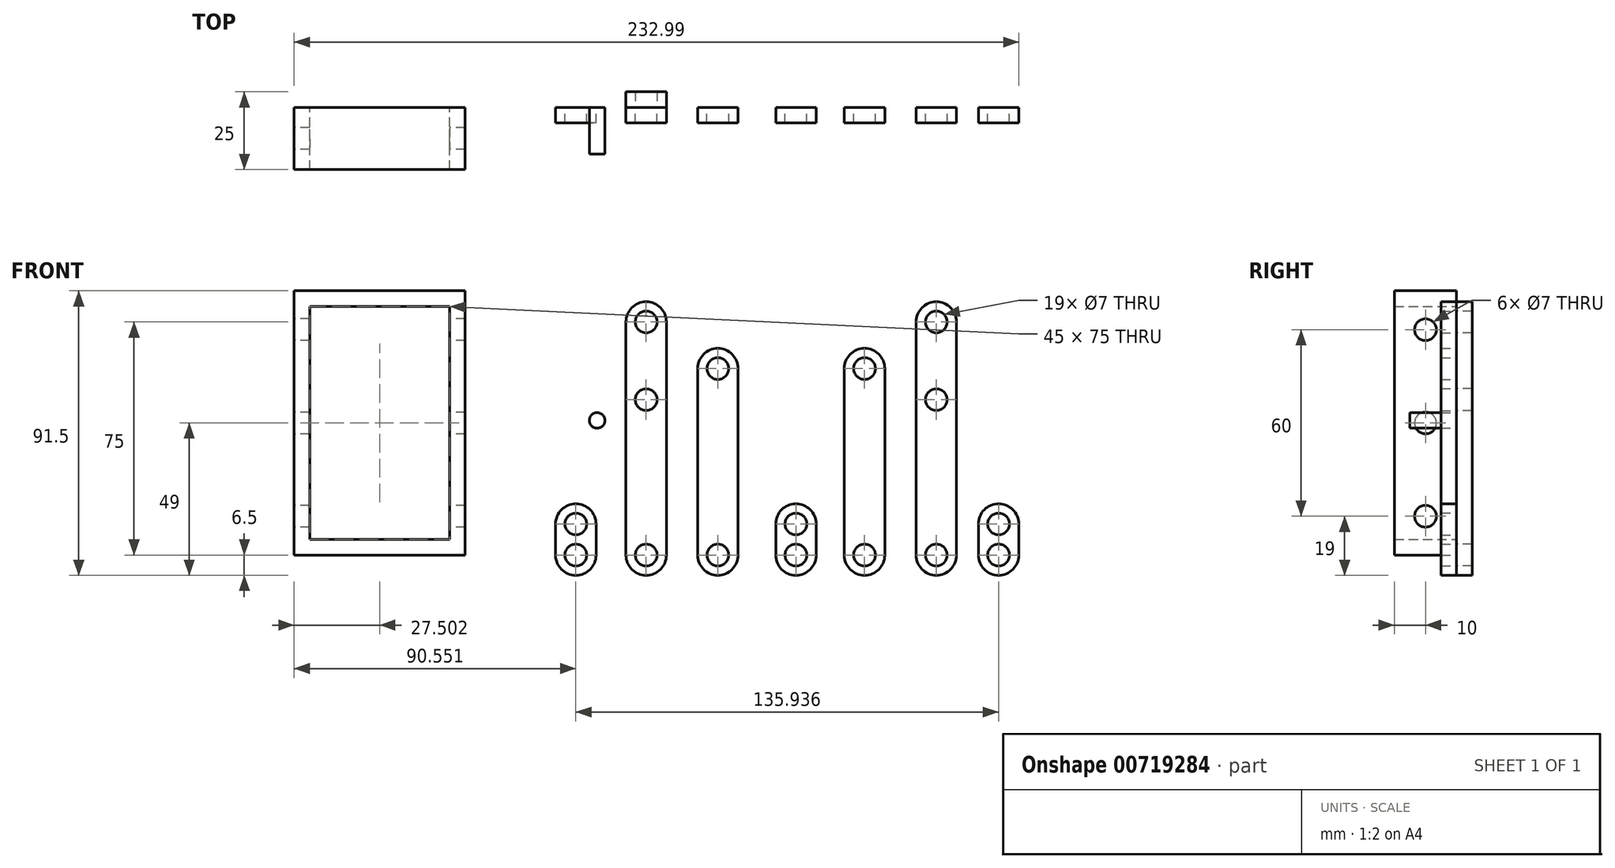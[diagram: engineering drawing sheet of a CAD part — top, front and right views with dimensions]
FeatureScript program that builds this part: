
annotation { "Feature Type Name" : "Feature", "Feature Type Description" : "" }
export const myFeature = defineFeature(function(context is Context, id is Id, definition is map)
    precondition{}
    {
        {
            assignVariable(context, id + "F0", {"name" : "D", "anyValue" : 5});
        }
        {
            var Q0;
            Q0=qCreatedBy(makeId("Front.planeOp"),FACE);
            var sketch = newSketch(context, id + "F1", { "sketchPlane" : qUnion([Q0])});
            skLineSegment(sketch, "E0", {"start": v(3.36, 0) * mm, "end": v(3.36, 10) * mm});
            skLineSegment(sketch, "E1", {"start": v(16.36, 10) * mm, "end": v(16.36, 0) * mm});
            skArc(sketch, "E2", {"start": v(16.36, 10) * mm, "mid": v(9.86, 16.5) * mm, "end": v(3.36, 10) * mm});
            skArc(sketch, "E3", {"start": v(3.36, 0) * mm, "mid": v(9.86, -6.5) * mm, "end": v(16.36, 0) * mm});
            skCircle(sketch, "E4", {"center": v(9.86, 10) * mm, "radius": 3.5 * mm});
            skCircle(sketch, "E5", {"center": v(9.86, 0) * mm, "radius": 3.5 * mm});
            skLineSegment(sketch, "E6", {"start": v(25.98, 0) * mm, "end": v(25.98, 75) * mm});
            skLineSegment(sketch, "E7", {"start": v(38.98, 75) * mm, "end": v(38.98, 0) * mm});
            skArc(sketch, "E8", {"start": v(38.98, 75) * mm, "mid": v(32.48, 81.5) * mm, "end": v(25.98, 75) * mm});
            skArc(sketch, "E9", {"start": v(25.98, 0) * mm, "mid": v(32.48, -6.5) * mm, "end": v(38.98, 0) * mm});
            skCircle(sketch, "E10", {"center": v(32.48, 75) * mm, "radius": 3.5 * mm});
            skCircle(sketch, "E11", {"center": v(32.48, 0) * mm, "radius": 3.5 * mm});
            skCircle(sketch, "E12", {"center": v(32.48, 50) * mm, "radius": 3.5 * mm});
            skLineSegment(sketch, "E13", {"start": v(49.03, 0) * mm, "end": v(49.03, 60) * mm});
            skLineSegment(sketch, "E14", {"start": v(62.03, 60) * mm, "end": v(62.03, 0) * mm});
            skArc(sketch, "E15", {"start": v(62.03, 60) * mm, "mid": v(55.53, 66.5) * mm, "end": v(49.03, 60) * mm});
            skArc(sketch, "E16", {"start": v(49.03, 0) * mm, "mid": v(55.53, -6.5) * mm, "end": v(62.03, 0) * mm});
            skCircle(sketch, "E17", {"center": v(55.53, 60) * mm, "radius": 3.5 * mm});
            skCircle(sketch, "E18", {"center": v(55.53, 0) * mm, "radius": 3.5 * mm});
            skLineSegment(sketch, "E19", {"start": v(74.13, 0) * mm, "end": v(74.13, 10) * mm});
            skLineSegment(sketch, "E20", {"start": v(87.13, 10) * mm, "end": v(87.13, 0) * mm});
            skArc(sketch, "E21", {"start": v(87.13, 10) * mm, "mid": v(80.63, 16.5) * mm, "end": v(74.13, 10) * mm});
            skArc(sketch, "E22", {"start": v(74.13, 0) * mm, "mid": v(80.63, -6.5) * mm, "end": v(87.13, 0) * mm});
            skCircle(sketch, "E23", {"center": v(80.63, 10) * mm, "radius": 3.5 * mm});
            skCircle(sketch, "E24", {"center": v(80.63, 0) * mm, "radius": 3.5 * mm});
            skLineSegment(sketch, "E25", {"start": v(96.2, 0) * mm, "end": v(96.2, 60) * mm});
            skLineSegment(sketch, "E26", {"start": v(109.2, 60) * mm, "end": v(109.2, 0) * mm});
            skArc(sketch, "E27", {"start": v(109.2, 60) * mm, "mid": v(102.7, 66.5) * mm, "end": v(96.2, 60) * mm});
            skArc(sketch, "E28", {"start": v(96.2, 0) * mm, "mid": v(102.7, -6.5) * mm, "end": v(109.2, 0) * mm});
            skCircle(sketch, "E29", {"center": v(102.7, 60) * mm, "radius": 3.5 * mm});
            skCircle(sketch, "E30", {"center": v(102.7, 0) * mm, "radius": 3.5 * mm});
            skLineSegment(sketch, "E31", {"start": v(119.27, 0) * mm, "end": v(119.27, 75) * mm});
            skLineSegment(sketch, "E32", {"start": v(132.27, 75) * mm, "end": v(132.27, 0) * mm});
            skArc(sketch, "E33", {"start": v(132.27, 75) * mm, "mid": v(125.77, 81.5) * mm, "end": v(119.27, 75) * mm});
            skArc(sketch, "E34", {"start": v(119.27, 0) * mm, "mid": v(125.77, -6.5) * mm, "end": v(132.27, 0) * mm});
            skCircle(sketch, "E35", {"center": v(125.77, 75) * mm, "radius": 3.5 * mm});
            skCircle(sketch, "E36", {"center": v(125.77, 0) * mm, "radius": 3.5 * mm});
            skCircle(sketch, "E37", {"center": v(125.77, 50) * mm, "radius": 3.5 * mm});
            skLineSegment(sketch, "E38", {"start": v(139.3, 0) * mm, "end": v(139.3, 10) * mm});
            skLineSegment(sketch, "E39", {"start": v(152.3, 10) * mm, "end": v(152.3, 0) * mm});
            skArc(sketch, "E40", {"start": v(152.3, 10) * mm, "mid": v(145.8, 16.5) * mm, "end": v(139.3, 10) * mm});
            skArc(sketch, "E41", {"start": v(139.3, 0) * mm, "mid": v(145.8, -6.5) * mm, "end": v(152.3, 0) * mm});
            skCircle(sketch, "E42", {"center": v(145.8, 10) * mm, "radius": 3.5 * mm});
            skCircle(sketch, "E43", {"center": v(145.8, 0) * mm, "radius": 3.5 * mm});
            skSolve(sketch);
        }
        {
            var Q0;
            Q0 = qSketchRegion(id + "F1", true);
            extrude(context, id + "F2", {"entities" : qUnion([Q0]), "depth" : (getVariable(context, 'D')) * mm, "offsetDistance" : 25 * mm});
        }
        {
            var Q0;
            Q0=qCreatedBy(makeId("Front.planeOp"),FACE);
            var sketch = newSketch(context, id + "F3", { "sketchPlane" : qUnion([Q0])});
            skCircle(sketch, "E44", {"center": v(16.71, 43.3) * mm, "radius": 2.5 * mm});
            skSolve(sketch);
        }
        {
            var Q0;
            Q0=makeQuery(id+"F3.imprint","IMPRINT",FACE,{"disambiguationData":[TD([[makeQuery(id+"F3.imprint","IMPRINT",EDGE,{"derivedFrom":sQuery(id+"F3.wireOp",EDGE,"E44")}),1.0]])]});
            extrude(context, id + "F4", {"entities" : qUnion([Q0]), "depth" : 15 * mm, "offsetDistance" : 25 * mm});
        }
        {
            var Q0;
            Q0=qCreatedBy(makeId("Front.planeOp"),FACE);
            var sketch = newSketch(context, id + "F5", { "sketchPlane" : qUnion([Q0])});
            skLineSegment(sketch, "E45.bottom", {"start": v(-75.69, 80) * mm, "end": v(-30.69, 80) * mm});
            skLineSegment(sketch, "E45.top", {"start": v(-75.69, 5) * mm, "end": v(-30.69, 5) * mm});
            skLineSegment(sketch, "E45.left", {"start": v(-75.69, 80) * mm, "end": v(-75.69, 5) * mm});
            skLineSegment(sketch, "E45.right", {"start": v(-30.69, 80) * mm, "end": v(-30.69, 5) * mm});
            skPoint(sketch, "E46.middle", {"position": v(-53.19, 42.5) * mm});
            skPoint(sketch, "E46.middle.positionSnap0", {"position": v(-53.19, 80) * mm});
            skPoint(sketch, "E46.middle.positionSnap1", {"position": v(-75.69, 42.5) * mm});
            skLineSegment(sketch, "E47.0", {"start": v(-80.69, 85) * mm, "end": v(-80.69, 0) * mm});
            skLineSegment(sketch, "E47.1", {"start": v(-80.69, 85) * mm, "end": v(-25.69, 85) * mm});
            skLineSegment(sketch, "E47.2", {"start": v(-25.69, 85) * mm, "end": v(-25.69, 0) * mm});
            skLineSegment(sketch, "E47.3", {"start": v(-80.69, 0) * mm, "end": v(-25.69, 0) * mm});
            skSolve(sketch);
        }
        {
            var Q0;
            Q0 = qSketchRegion(id + "F5", true);
            extrude(context, id + "F6", {"entities" : qUnion([Q0]), "depth" : 20 * mm, "offsetDistance" : 25 * mm});
        }
        {
            var Q0;
            Q0=makeQuery(id+"F6.opExtrude","SWEPT_FACE",FACE,{"disambiguationData":[OSD([sQuery(id+"F5.wireOp",EDGE,"E47.0")])]});
            var sketch = newSketch(context, id + "F7", { "sketchPlane" : qUnion([Q0])});
            skCircle(sketch, "E48", {"center": v(10, 72.5) * mm, "radius": 3.5 * mm});
            skCircle(sketch, "E49", {"center": v(10, 42.5) * mm, "radius": 3.5 * mm});
            skCircle(sketch, "E50", {"center": v(10, 12.5) * mm, "radius": 3.5 * mm});
            skSolve(sketch);
        }
        {
            var Q0;
            Q0=makeQuery(id+"F7.imprint","IMPRINT",FACE,{"disambiguationData":[TD([[makeQuery(id+"F7.imprint","IMPRINT",EDGE,{"derivedFrom":sQuery(id+"F7.wireOp",EDGE,"E48")}),1.0]])]});
            var Q1;
            Q1=makeQuery(id+"F7.imprint","IMPRINT",FACE,{"disambiguationData":[TD([[makeQuery(id+"F7.imprint","IMPRINT",EDGE,{"derivedFrom":sQuery(id+"F7.wireOp",EDGE,"E49")}),1.0]])]});
            var Q2;
            Q2=makeQuery(id+"F7.imprint","IMPRINT",FACE,{"disambiguationData":[TD([[makeQuery(id+"F7.imprint","IMPRINT",EDGE,{"derivedFrom":sQuery(id+"F7.wireOp",EDGE,"E50")}),1.0]])]});
            var Q3;
            Q3=makeQuery(id+"F6.opExtrude","SWEPT_FACE",FACE,{"disambiguationData":[OSD([sQuery(id+"F5.wireOp",EDGE,"E47.2")])]});
            extrude(context, id + "F8", {"entities" : qUnion([Q0, Q1, Q2]), "operationType" : NewBodyOperationType.REMOVE, "endBound" : BoundingType.UP_TO_SURFACE, "oppositeDirection" : true, "depth" : 25 * mm, "endBoundEntityFace" : qUnion([Q3]), "offsetDistance" : 25 * mm});
        }
        {
            var Q0;
            Q0=makeQuery(id+"F2.opExtrude","SWEPT_BODY",BODY,{"disambiguationData":[OSD([sQuery(id+"F1.wireOp",EDGE,"E6"),sQuery(id+"F1.wireOp",EDGE,"E7"),sQuery(id+"F1.wireOp",EDGE,"E8"),sQuery(id+"F1.wireOp",EDGE,"E9"),sQuery(id+"F1.wireOp",EDGE,"E10"),sQuery(id+"F1.wireOp",EDGE,"E11"),sQuery(id+"F1.wireOp",EDGE,"E12")])]});
            var Q1;
            Q1=qCreatedBy(makeId("Front.planeOp"),FACE);
            mirror(context, id + "F9", {"operationType" : NewBodyOperationType.ADD, "entities" : qUnion([Q0]), "mirrorPlane" : qUnion([Q1])});
        }
    });
